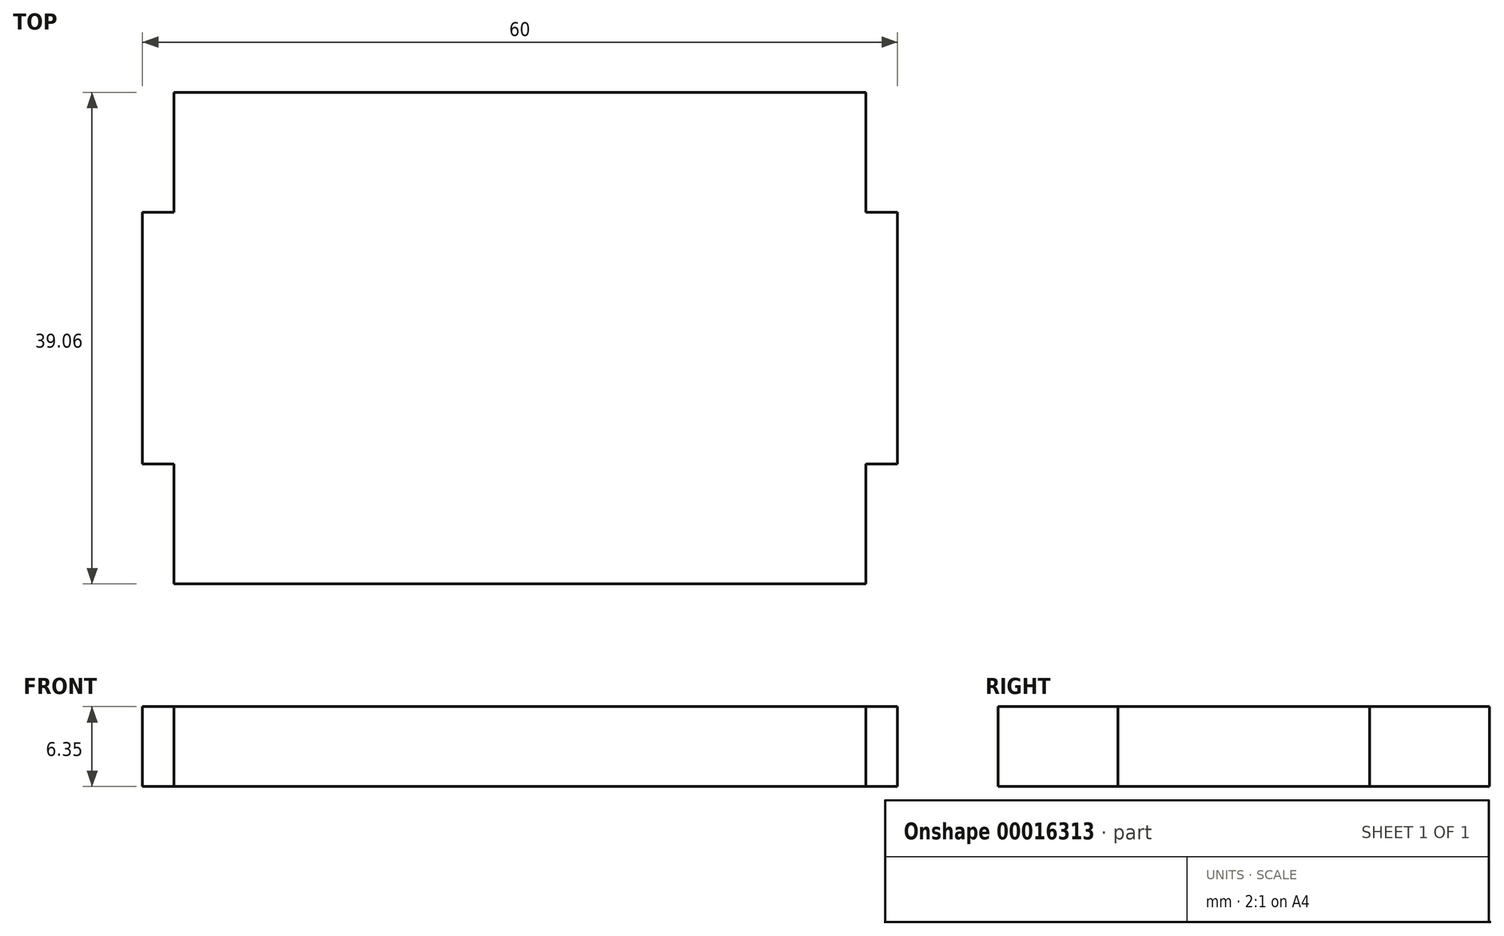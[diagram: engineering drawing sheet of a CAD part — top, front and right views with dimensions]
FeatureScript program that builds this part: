
annotation { "Feature Type Name" : "Feature", "Feature Type Description" : "" }
export const myFeature = defineFeature(function(context is Context, id is Id, definition is map)
    precondition{}
    {
        {
            var Q0;
            Q0=qCreatedBy(makeId("Top.planeOp"),FACE);
            var sketch = newSketch(context, id + "F0", { "sketchPlane" : qUnion([Q0])});
            skLineSegment(sketch, "E0.rect.bottom", {"start": v(30, 10) * mm, "end": v(27.5, 10) * mm});
            skLineSegment(sketch, "E0.rect.top", {"start": v(30, -10) * mm, "end": v(27.5, -10) * mm});
            skLineSegment(sketch, "E0.rect.left", {"start": v(30, 10) * mm, "end": v(30, -10) * mm});
            skLineSegment(sketch, "E0.rect.right", {"start": v(-30, 10) * mm, "end": v(-30, -10) * mm});
            skPoint(sketch, "E0.rect.middle", {"position": v(0, 0) * mm});
            skLineSegment(sketch, "E1.rect.bottom", {"start": v(27.5, 19.53) * mm, "end": v(-27.5, 19.53) * mm});
            skLineSegment(sketch, "E1.rect.top", {"start": v(27.5, -19.53) * mm, "end": v(-27.5, -19.53) * mm});
            skLineSegment(sketch, "E1.rect.left", {"start": v(27.5, 19.53) * mm, "end": v(27.5, 10) * mm});
            skLineSegment(sketch, "E1.rect.right", {"start": v(-27.5, 19.53) * mm, "end": v(-27.5, 10) * mm});
            skLineSegment(sketch, "E2.trimOffspring", {"start": v(-27.5, 10) * mm, "end": v(-30, 10) * mm});
            skLineSegment(sketch, "E3.trimOffspring", {"start": v(-27.5, -10) * mm, "end": v(-27.5, -19.53) * mm});
            skLineSegment(sketch, "E4.trimOffspring", {"start": v(-27.5, -10) * mm, "end": v(-30, -10) * mm});
            skLineSegment(sketch, "E5.trimOffspring", {"start": v(27.5, -10) * mm, "end": v(27.5, -19.53) * mm});
            skLineSegment(sketch, "E6", {"start": v(-30, 0) * mm, "end": v(30, 0) * mm, "construction": true});
            skLineSegment(sketch, "E7", {"start": v(0, 19.53) * mm, "end": v(0, -19.53) * mm, "construction": true});
            skSolve(sketch);
        }
        {
            var Q0;
            Q0=makeQuery(id+"F0.imprint","IMPRINT",FACE,{"disambiguationData":[TD([[makeQuery(id+"F0.imprint","IMPRINT",EDGE,{"derivedFrom":sQuery(id+"F0.wireOp",EDGE,"E0.rect.bottom")}),1.0]])]});
            extrude(context, id + "F1", {"entities" : qUnion([Q0]), "depth" : 6.35 * mm});
        }
    });
